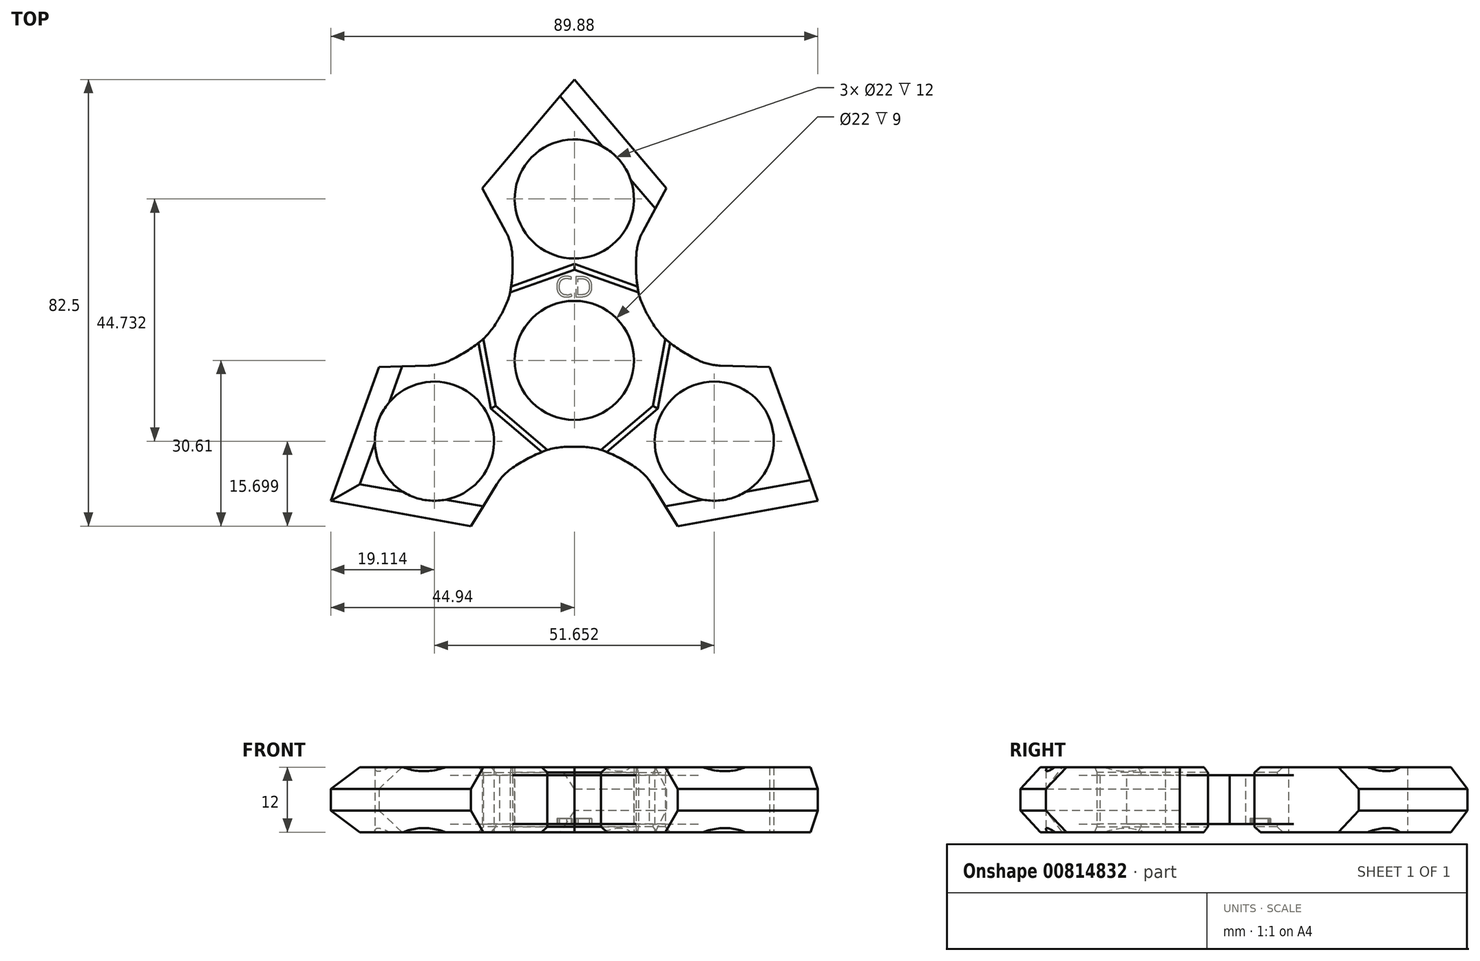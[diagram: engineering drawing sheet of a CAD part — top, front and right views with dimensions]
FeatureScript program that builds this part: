
annotation { "Feature Type Name" : "Feature", "Feature Type Description" : "" }
export const myFeature = defineFeature(function(context is Context, id is Id, definition is map)
    precondition{}
    {
        {
            var Q0;
            Q0=qCreatedBy(makeId("Top.planeOp"),FACE);
            var sketch = newSketch(context, id + "F0", { "sketchPlane" : qUnion([Q0])});
            skCircle(sketch, "E0", {"center": v(0, 0) * mm, "radius": 11 * mm});
            skCircle(sketch, "E1", {"center": v(0, 0) * mm, "radius": 15 * mm});
            skPoint(sketch, "E2.visualSharp", {"position": v(-8.6, 40.5) * mm});
            skPoint(sketch, "E3.MirrorP", {"position": v(8.6, 40.5) * mm});
            skLineSegment(sketch, "E4", {"start": v(0, 51.9) * mm, "end": v(-16.97, 31.83) * mm});
            skLineSegment(sketch, "E5", {"start": v(-16.97, 31.83) * mm, "end": v(-12.64, 23.8) * mm});
            skLineSegment(sketch, "E6.MirrorCS", {"start": v(0, 51.9) * mm, "end": v(16.97, 31.83) * mm});
            skArc(sketch, "E7", {"start": v(-13.91, 5.61) * mm, "mid": v(-11.83, 12.55) * mm, "end": v(-11.47, 19.78) * mm});
            skLineSegment(sketch, "E8.MirrorCS", {"start": v(16.97, 31.83) * mm, "end": v(12.64, 23.8) * mm});
            skArc(sketch, "E9.MirrorCS", {"start": v(13.91, 5.61) * mm, "mid": v(11.83, 12.55) * mm, "end": v(11.47, 19.78) * mm});
            skPoint(sketch, "E10.visualSharp", {"position": v(-11.73, 22.12) * mm});
            skArc(sketch, "E10.filletArc", {"start": v(-11.47, 19.78) * mm, "mid": v(-11.84, 21.85) * mm, "end": v(-12.64, 23.8) * mm});
            skPoint(sketch, "E11.visualSharp", {"position": v(11.73, 22.12) * mm});
            skArc(sketch, "E11.filletArc", {"start": v(12.64, 23.8) * mm, "mid": v(11.84, 21.85) * mm, "end": v(11.47, 19.78) * mm});
            skPoint(sketch, "E12.1.1", {"position": v(-30.77, -27.69) * mm});
            skPoint(sketch, "E12.1.2", {"position": v(-13.29, -21.22) * mm});
            skPoint(sketch, "E12.1.4", {"position": v(-25.02, -0.9) * mm});
            skLineSegment(sketch, "E12.1.5", {"start": v(-44.94, -25.95) * mm, "end": v(-36.05, -1.22) * mm});
            skLineSegment(sketch, "E12.1.6", {"start": v(-36.05, -1.22) * mm, "end": v(-26.94, -0.95) * mm});
            skLineSegment(sketch, "E12.1.7", {"start": v(-19.08, -30.6) * mm, "end": v(-14.3, -22.85) * mm});
            skLineSegment(sketch, "E12.1.9", {"start": v(-44.94, -25.95) * mm, "end": v(-19.08, -30.6) * mm});
            skPoint(sketch, "E12.1.10", {"position": v(-39.36, -12.8) * mm});
            skArc(sketch, "E12.1.12", {"start": v(-26.94, -0.95) * mm, "mid": v(-24.85, -0.67) * mm, "end": v(-22.86, 0.04) * mm});
            skArc(sketch, "E12.1.13", {"start": v(-11.4, -19.82) * mm, "mid": v(-13, -21.18) * mm, "end": v(-14.3, -22.85) * mm});
            skArc(sketch, "E12.1.14", {"start": v(2.1, -14.85) * mm, "mid": v(-4.95, -16.51) * mm, "end": v(-11.4, -19.82) * mm});
            skArc(sketch, "E12.1.15", {"start": v(-11.82, 9.24) * mm, "mid": v(-16.78, 3.97) * mm, "end": v(-22.86, 0.04) * mm});
            skPoint(sketch, "E12.2.1", {"position": v(39.36, -12.8) * mm});
            skPoint(sketch, "E12.2.2", {"position": v(25.02, -0.9) * mm});
            skPoint(sketch, "E12.2.4", {"position": v(13.29, -21.22) * mm});
            skLineSegment(sketch, "E12.2.5", {"start": v(44.94, -25.95) * mm, "end": v(19.08, -30.6) * mm});
            skLineSegment(sketch, "E12.2.6", {"start": v(19.08, -30.6) * mm, "end": v(14.3, -22.85) * mm});
            skLineSegment(sketch, "E12.2.7", {"start": v(36.05, -1.22) * mm, "end": v(26.94, -0.95) * mm});
            skLineSegment(sketch, "E12.2.9", {"start": v(44.94, -25.95) * mm, "end": v(36.05, -1.22) * mm});
            skPoint(sketch, "E12.2.10", {"position": v(30.77, -27.69) * mm});
            skArc(sketch, "E12.2.12", {"start": v(14.3, -22.85) * mm, "mid": v(13, -21.18) * mm, "end": v(11.4, -19.82) * mm});
            skArc(sketch, "E12.2.13", {"start": v(22.86, 0.04) * mm, "mid": v(24.85, -0.67) * mm, "end": v(26.94, -0.95) * mm});
            skArc(sketch, "E12.2.14", {"start": v(11.82, 9.24) * mm, "mid": v(16.78, 3.97) * mm, "end": v(22.86, 0.04) * mm});
            skArc(sketch, "E12.2.15", {"start": v(-2.1, -14.85) * mm, "mid": v(4.95, -16.51) * mm, "end": v(11.4, -19.82) * mm});
            skArc(sketch, "E13", {"start": v(0, -15.94) * mm, "mid": v(-2.5, -16.04) * mm, "end": v(-4.95, -16.51) * mm});
            skArc(sketch, "E14.MirrorCS", {"start": v(0, -15.94) * mm, "mid": v(2.5, -16.04) * mm, "end": v(4.95, -16.51) * mm});
            skArc(sketch, "E15.1.1", {"start": v(13.8, 7.97) * mm, "mid": v(12.64, 10.18) * mm, "end": v(11.83, 12.55) * mm});
            skArc(sketch, "E15.1.2", {"start": v(13.8, 7.97) * mm, "mid": v(15.14, 5.85) * mm, "end": v(16.78, 3.97) * mm});
            skArc(sketch, "E15.2.1", {"start": v(-13.8, 7.97) * mm, "mid": v(-15.14, 5.85) * mm, "end": v(-16.78, 3.97) * mm});
            skArc(sketch, "E15.2.2", {"start": v(-13.8, 7.97) * mm, "mid": v(-12.64, 10.18) * mm, "end": v(-11.83, 12.55) * mm});
            skCircle(sketch, "E16", {"center": v(0, 29.82) * mm, "radius": 11 * mm});
            skCircle(sketch, "E17.1.0", {"center": v(-25.83, -14.91) * mm, "radius": 11 * mm});
            skCircle(sketch, "E17.2.0", {"center": v(25.83, -14.91) * mm, "radius": 11 * mm});
            skSolve(sketch);
        }
        {
            var Q0;
            Q0 = qSketchRegion(id + "F0", true);
            extrude(context, id + "F1", {"entities" : qUnion([Q0]), "depth" : 9 * mm, "offsetDistance" : 25 * mm});
        }
        {
            var Q0;
            Q0=makeQuery(id+"F4rAhD535oqGD43_1.opFillet","SPLIT",FACE,{"disambiguationData":[OD(0.0)],"derivedFrom":makeQuery(id+"FJmebITgFN1S2HH_1.opChamfer","SPLIT",FACE,{"disambiguationData":[OD(3.0)],"derivedFrom":makeQuery(id+"F1.opExtrude","CAP_FACE",FACE,{"disambiguationData":[OSD([sQuery(id+"F0.wireOp",EDGE,"E1"),sQuery(id+"F0.wireOp",EDGE,"wFqUF3aU-xvko-5oIi-hobR-WI0LvXs7SEYY"),sQuery(id+"F0.wireOp",EDGE,"E4"),sQuery(id+"F0.wireOp",EDGE,"E5"),sQuery(id+"F0.wireOp",EDGE,"E6.MirrorCS"),sQuery(id+"F0.wireOp",EDGE,"E7"),sQuery(id+"F0.wireOp",EDGE,"E8.MirrorCS"),sQuery(id+"F0.wireOp",EDGE,"E9.MirrorCS"),sQuery(id+"F0.wireOp",EDGE,"E10.filletArc"),sQuery(id+"F0.wireOp",EDGE,"E11.filletArc"),sQuery(id+"F0.wireOp",EDGE,"xOrXqrbk-GGfu-HfVZ-Al4d-8NAzLdtHC7hU"),sQuery(id+"F0.wireOp",EDGE,"3626fe40-44d3-4f9b-b4e5-6d0232d855d70.MirrorCS"),sQuery(id+"F0.wireOp",EDGE,"E12.1.3"),sQuery(id+"F0.wireOp",EDGE,"E12.1.5"),sQuery(id+"F0.wireOp",EDGE,"E12.1.6"),sQuery(id+"F0.wireOp",EDGE,"E12.1.7"),sQuery(id+"F0.wireOp",EDGE,"E12.1.8"),sQuery(id+"F0.wireOp",EDGE,"E12.1.9"),sQuery(id+"F0.wireOp",EDGE,"E12.1.11"),sQuery(id+"F0.wireOp",EDGE,"E12.1.12"),sQuery(id+"F0.wireOp",EDGE,"E12.1.13"),sQuery(id+"F0.wireOp",EDGE,"E12.1.14"),sQuery(id+"F0.wireOp",EDGE,"E12.1.15"),sQuery(id+"F0.wireOp",EDGE,"E12.2.3"),sQuery(id+"F0.wireOp",EDGE,"E12.2.5"),sQuery(id+"F0.wireOp",EDGE,"E12.2.6"),sQuery(id+"F0.wireOp",EDGE,"E12.2.7"),sQuery(id+"F0.wireOp",EDGE,"E12.2.8"),sQuery(id+"F0.wireOp",EDGE,"E12.2.9"),sQuery(id+"F0.wireOp",EDGE,"E12.2.11"),sQuery(id+"F0.wireOp",EDGE,"E12.2.12"),sQuery(id+"F0.wireOp",EDGE,"E12.2.13"),sQuery(id+"F0.wireOp",EDGE,"E12.2.14"),sQuery(id+"F0.wireOp",EDGE,"E12.2.15"),sQuery(id+"F0.wireOp",EDGE,"E13"),sQuery(id+"F0.wireOp",EDGE,"E14.MirrorCS"),sQuery(id+"F0.wireOp",EDGE,"E15.1.1"),sQuery(id+"F0.wireOp",EDGE,"E15.1.2"),sQuery(id+"F0.wireOp",EDGE,"E15.2.1"),sQuery(id+"F0.wireOp",EDGE,"E15.2.2")])],"isStart":false})})});
            var sketch = newSketch(context, id + "F2", { "sketchPlane" : qUnion([Q0])});
            skCircle(sketch, "E18", {"center": v(0, 0) * mm, "radius": 11 * mm});
            skCircle(sketch, "E19", {"center": v(0, 0) * mm, "radius": 15.25 * mm});
            skSolve(sketch);
        }
        {
            var Q0;
            Q0 = qSketchRegion(id + "F2", true);
            extrude(context, id + "F3", {"entities" : qUnion([Q0]), "operationType" : NewBodyOperationType.ADD, "oppositeDirection" : true, "depth" : 9 * mm, "offsetDistance" : 25 * mm});
        }
        {
            var Q0;
            Q0=makeQuery(id+"F3.boolean.opBoolean","MERGE",FACE,{"derivedFrom":[makeQuery(id+"F1.opExtrude","CAP_FACE",FACE,{"disambiguationData":[OSD([sQuery(id+"F0.wireOp",EDGE,"E1"),sQuery(id+"F0.wireOp",EDGE,"E4"),sQuery(id+"F0.wireOp",EDGE,"E5"),sQuery(id+"F0.wireOp",EDGE,"E6.MirrorCS"),sQuery(id+"F0.wireOp",EDGE,"E7"),sQuery(id+"F0.wireOp",EDGE,"E8.MirrorCS"),sQuery(id+"F0.wireOp",EDGE,"E9.MirrorCS"),sQuery(id+"F0.wireOp",EDGE,"E10.filletArc"),sQuery(id+"F0.wireOp",EDGE,"E11.filletArc"),sQuery(id+"F0.wireOp",EDGE,"E12.1.5"),sQuery(id+"F0.wireOp",EDGE,"E12.1.6"),sQuery(id+"F0.wireOp",EDGE,"E12.1.7"),sQuery(id+"F0.wireOp",EDGE,"E12.1.9"),sQuery(id+"F0.wireOp",EDGE,"E12.1.12"),sQuery(id+"F0.wireOp",EDGE,"E12.1.13"),sQuery(id+"F0.wireOp",EDGE,"E12.1.14"),sQuery(id+"F0.wireOp",EDGE,"E12.1.15"),sQuery(id+"F0.wireOp",EDGE,"E12.2.5"),sQuery(id+"F0.wireOp",EDGE,"E12.2.6"),sQuery(id+"F0.wireOp",EDGE,"E12.2.7"),sQuery(id+"F0.wireOp",EDGE,"E12.2.9"),sQuery(id+"F0.wireOp",EDGE,"E12.2.12"),sQuery(id+"F0.wireOp",EDGE,"E12.2.13"),sQuery(id+"F0.wireOp",EDGE,"E12.2.14"),sQuery(id+"F0.wireOp",EDGE,"E12.2.15"),sQuery(id+"F0.wireOp",EDGE,"E13"),sQuery(id+"F0.wireOp",EDGE,"E14.MirrorCS"),sQuery(id+"F0.wireOp",EDGE,"E15.1.1"),sQuery(id+"F0.wireOp",EDGE,"E15.1.2"),sQuery(id+"F0.wireOp",EDGE,"E15.2.1"),sQuery(id+"F0.wireOp",EDGE,"E15.2.2"),sQuery(id+"F0.wireOp",EDGE,"E16"),sQuery(id+"F0.wireOp",EDGE,"E17.1.0"),sQuery(id+"F0.wireOp",EDGE,"E17.2.0")])],"isStart":false}),makeQuery(id+"F3.opExtrude","CAP_FACE",FACE,{"disambiguationData":[OSD([sQuery(id+"F2.wireOp",EDGE,"E18"),sQuery(id+"F2.wireOp",EDGE,"E19")])],"isStart":true})]});
            var sketch = newSketch(context, id + "F4", { "sketchPlane" : qUnion([Q0])});
            skLineSegment(sketch, "E20", {"start": v(-36.05, -1.22) * mm, "end": v(-44.94, -25.95) * mm});
            skLineSegment(sketch, "E21", {"start": v(-26.94, -0.95) * mm, "end": v(-36.05, -1.22) * mm});
            skArc(sketch, "E22", {"start": v(-26.94, -0.95) * mm, "mid": v(-24.85, -0.67) * mm, "end": v(-22.86, 0.04) * mm});
            skArc(sketch, "E23", {"start": v(-22.86, 0.04) * mm, "mid": v(-19.7, 1.8) * mm, "end": v(-16.78, 3.97) * mm});
            skArc(sketch, "E24.MirrorCS", {"start": v(-11.4, -19.82) * mm, "mid": v(-8.28, -17.96) * mm, "end": v(-4.95, -16.51) * mm});
            skArc(sketch, "E25.MirrorCS", {"start": v(-14.3, -22.85) * mm, "mid": v(-13, -21.18) * mm, "end": v(-11.4, -19.82) * mm});
            skLineSegment(sketch, "E26.MirrorCS", {"start": v(-14.3, -22.85) * mm, "end": v(-19.08, -30.6) * mm});
            skLineSegment(sketch, "E27.MirrorCS", {"start": v(-19.08, -30.6) * mm, "end": v(-44.94, -25.95) * mm});
            skLineSegment(sketch, "E28", {"start": v(-16.78, 3.97) * mm, "end": v(-14.5, -8.37) * mm});
            skLineSegment(sketch, "E29", {"start": v(-14.5, -8.37) * mm, "end": v(-4.95, -16.51) * mm});
            skCircle(sketch, "E30", {"center": v(-25.83, -14.91) * mm, "radius": 11 * mm});
            skLineSegment(sketch, "E31.1.0", {"start": v(19.08, -30.6) * mm, "end": v(44.94, -25.95) * mm});
            skLineSegment(sketch, "E31.1.1", {"start": v(26.94, -0.95) * mm, "end": v(36.05, -1.22) * mm});
            skLineSegment(sketch, "E31.1.2", {"start": v(14.5, -8.37) * mm, "end": v(16.78, 3.97) * mm});
            skCircle(sketch, "E31.1.3", {"center": v(25.83, -14.91) * mm, "radius": 11 * mm});
            skArc(sketch, "E31.1.4", {"start": v(14.3, -22.85) * mm, "mid": v(13, -21.18) * mm, "end": v(11.4, -19.82) * mm});
            skLineSegment(sketch, "E31.1.5", {"start": v(36.05, -1.22) * mm, "end": v(44.94, -25.95) * mm});
            skLineSegment(sketch, "E31.1.6", {"start": v(4.95, -16.51) * mm, "end": v(14.5, -8.37) * mm});
            skArc(sketch, "E31.1.7", {"start": v(11.4, -19.82) * mm, "mid": v(8.28, -17.96) * mm, "end": v(4.95, -16.51) * mm});
            skLineSegment(sketch, "E31.1.8", {"start": v(14.3, -22.85) * mm, "end": v(19.08, -30.6) * mm});
            skArc(sketch, "E31.1.9", {"start": v(26.94, -0.95) * mm, "mid": v(24.85, -0.67) * mm, "end": v(22.86, 0.04) * mm});
            skArc(sketch, "E31.1.10", {"start": v(22.86, 0.04) * mm, "mid": v(19.7, 1.8) * mm, "end": v(16.78, 3.97) * mm});
            skLineSegment(sketch, "E31.1.11", {"start": v(36.05, -1.22) * mm, "end": v(44.94, -25.95) * mm});
            skLineSegment(sketch, "E31.1.12", {"start": v(36.05, -1.22) * mm, "end": v(44.94, -25.95) * mm});
            skLineSegment(sketch, "E31.2.0", {"start": v(16.97, 31.83) * mm, "end": v(0, 51.9) * mm});
            skLineSegment(sketch, "E31.2.1", {"start": v(-12.64, 23.8) * mm, "end": v(-16.97, 31.83) * mm});
            skLineSegment(sketch, "E31.2.2", {"start": v(0, 16.75) * mm, "end": v(-11.83, 12.55) * mm});
            skCircle(sketch, "E31.2.3", {"center": v(0, 29.82) * mm, "radius": 11 * mm});
            skArc(sketch, "E31.2.4", {"start": v(12.64, 23.8) * mm, "mid": v(11.84, 21.85) * mm, "end": v(11.47, 19.78) * mm});
            skLineSegment(sketch, "E31.2.5", {"start": v(-16.97, 31.83) * mm, "end": v(0, 51.9) * mm});
            skLineSegment(sketch, "E31.2.6", {"start": v(11.83, 12.55) * mm, "end": v(0, 16.75) * mm});
            skArc(sketch, "E31.2.7", {"start": v(11.47, 19.78) * mm, "mid": v(11.41, 16.15) * mm, "end": v(11.83, 12.55) * mm});
            skLineSegment(sketch, "E31.2.8", {"start": v(12.64, 23.8) * mm, "end": v(16.97, 31.83) * mm});
            skArc(sketch, "E31.2.9", {"start": v(-12.64, 23.8) * mm, "mid": v(-11.84, 21.85) * mm, "end": v(-11.47, 19.78) * mm});
            skArc(sketch, "E31.2.10", {"start": v(-11.47, 19.78) * mm, "mid": v(-11.41, 16.15) * mm, "end": v(-11.83, 12.55) * mm});
            skLineSegment(sketch, "E31.2.11", {"start": v(-16.97, 31.83) * mm, "end": v(0, 51.9) * mm});
            skLineSegment(sketch, "E31.2.12", {"start": v(-16.97, 31.83) * mm, "end": v(0, 51.9) * mm});
            skPoint(sketch, "E31.center", {"position": v(0, 0) * mm});
            skSolve(sketch);
        }
        {
            var Q0;
            Q0 = qSketchRegion(id + "F4", true);
            extrude(context, id + "F5", {"entities" : qUnion([Q0]), "operationType" : NewBodyOperationType.ADD, "depth" : 1.5 * mm, "offsetDistance" : 25 * mm, "hasSecondDirection" : true, "secondDirectionOppositeDirection" : true, "secondDirectionDepth" : 10.5 * mm});
        }
        {
            var Q0;
            Q0=makeQuery(id+"F5.opExtrude","CAP_EDGE",EDGE,{"disambiguationData":[OSD([sQuery(id+"F4.wireOp",EDGE,"E28")])],"isStart":false});
            var Q1;
            Q1=makeQuery(id+"F5.opExtrude","CAP_EDGE",EDGE,{"disambiguationData":[OSD([sQuery(id+"F4.wireOp",EDGE,"E29")])],"isStart":false});
            var Q2;
            Q2=makeQuery(id+"F5.opExtrude","CAP_EDGE",EDGE,{"disambiguationData":[OSD([sQuery(id+"F4.wireOp",EDGE,"E29")])],"isStart":true});
            var Q3;
            Q3=makeQuery(id+"F5.opExtrude","CAP_EDGE",EDGE,{"disambiguationData":[OSD([sQuery(id+"F4.wireOp",EDGE,"E28")])],"isStart":true});
            var Q4;
            Q4=makeQuery(id+"F5.opExtrude","CAP_EDGE",EDGE,{"disambiguationData":[OSD([sQuery(id+"F4.wireOp",EDGE,"E31.1.6")])],"isStart":true});
            var Q5;
            Q5=makeQuery(id+"F5.opExtrude","CAP_EDGE",EDGE,{"disambiguationData":[OSD([sQuery(id+"F4.wireOp",EDGE,"E31.1.2")])],"isStart":true});
            var Q6;
            Q6=makeQuery(id+"F5.opExtrude","CAP_EDGE",EDGE,{"disambiguationData":[OSD([sQuery(id+"F4.wireOp",EDGE,"E31.2.6")])],"isStart":true});
            var Q7;
            Q7=makeQuery(id+"F5.opExtrude","CAP_EDGE",EDGE,{"disambiguationData":[OSD([sQuery(id+"F4.wireOp",EDGE,"E31.2.2")])],"isStart":true});
            var Q8;
            Q8=makeQuery(id+"F5.opExtrude","CAP_EDGE",EDGE,{"disambiguationData":[OSD([sQuery(id+"F4.wireOp",EDGE,"E31.1.2")])],"isStart":false});
            var Q9;
            Q9=makeQuery(id+"F5.opExtrude","CAP_EDGE",EDGE,{"disambiguationData":[OSD([sQuery(id+"F4.wireOp",EDGE,"E31.1.6")])],"isStart":false});
            var Q10;
            Q10=makeQuery(id+"F5.opExtrude","CAP_EDGE",EDGE,{"disambiguationData":[OSD([sQuery(id+"F4.wireOp",EDGE,"E31.2.6")])],"isStart":false});
            var Q11;
            Q11=makeQuery(id+"F5.opExtrude","CAP_EDGE",EDGE,{"disambiguationData":[OSD([sQuery(id+"F4.wireOp",EDGE,"E31.2.2")])],"isStart":false});
            chamfer(context, id + "F6", {"entities" : qUnion([Q0, Q1, Q2, Q3, Q4, Q5, Q6, Q7, Q8, Q9, Q10, Q11]), "width" : 1 * mm, "tangentPropagation" : true});
        }
        {
            var Q0;
            Q0=makeQuery(id+"F5.opExtrude","CAP_EDGE",EDGE,{"disambiguationData":[OSD([sQuery(id+"F4.wireOp",EDGE,"E27.MirrorCS")])],"isStart":false});
            var Q1;
            Q1=makeQuery(id+"F5.opExtrude","CAP_EDGE",EDGE,{"disambiguationData":[OSD([sQuery(id+"F4.wireOp",EDGE,"E20")])],"isStart":false});
            var Q2;
            Q2=makeQuery(id+"F5.opExtrude","CAP_EDGE",EDGE,{"disambiguationData":[OSD([sQuery(id+"F4.wireOp",EDGE,"E27.MirrorCS")])],"isStart":true});
            var Q3;
            Q3=makeQuery(id+"F5.opExtrude","CAP_EDGE",EDGE,{"disambiguationData":[OSD([sQuery(id+"F4.wireOp",EDGE,"E20")])],"isStart":true});
            var Q4;
            Q4=makeQuery(id+"F5.opExtrude","CAP_EDGE",EDGE,{"disambiguationData":[OSD([sQuery(id+"F4.wireOp",EDGE,"E31.1.0")])],"isStart":false});
            var Q5;
            Q5=makeQuery(id+"F5.opExtrude","CAP_EDGE",EDGE,{"disambiguationData":[OSD([sQuery(id+"F4.wireOp",EDGE,"E31.1.0")])],"isStart":true});
            var Q6;
            Q6=makeQuery(id+"F5.opExtrude","CAP_EDGE",EDGE,{"disambiguationData":[OSD([sQuery(id+"F4.wireOp",EDGE,"E31.1.12")])],"isStart":false});
            var Q7;
            Q7=makeQuery(id+"F5.opExtrude","CAP_EDGE",EDGE,{"disambiguationData":[OSD([sQuery(id+"F4.wireOp",EDGE,"E31.1.12")])],"isStart":true});
            var Q8;
            Q8=makeQuery(id+"F5.opExtrude","CAP_EDGE",EDGE,{"disambiguationData":[OSD([sQuery(id+"F4.wireOp",EDGE,"E31.2.0")])],"isStart":false});
            var Q9;
            Q9=makeQuery(id+"F5.opExtrude","CAP_EDGE",EDGE,{"disambiguationData":[OSD([sQuery(id+"F4.wireOp",EDGE,"E31.2.0")])],"isStart":true});
            var Q10;
            Q10=makeQuery(id+"F5.opExtrude","CAP_EDGE",EDGE,{"disambiguationData":[OSD([sQuery(id+"F4.wireOp",EDGE,"E31.2.12")])],"isStart":true});
            var Q11;
            Q11=makeQuery(id+"F5.opExtrude","CAP_EDGE",EDGE,{"disambiguationData":[OSD([sQuery(id+"F4.wireOp",EDGE,"E31.2.12")])],"isStart":false});
            chamfer(context, id + "F7", {"entities" : qUnion([Q0, Q1, Q2, Q3, Q4, Q5, Q6, Q7, Q8, Q9, Q10, Q11]), "width" : 4 * mm, "tangentPropagation" : true});
        }
        {
            var Q0;
            {var subQ0=sQuery(id+"F2.wireOp",EDGE,"E18");var subQ1=makeQuery(id+"F3.opExtrude","CAP_FACE",FACE,{"disambiguationData":[OSD([subQ0,sQuery(id+"F2.wireOp",EDGE,"E19")])],"isStart":false});var subQ2=sQuery(id+"F0.wireOp",EDGE,"E15.2.2");var subQ3=sQuery(id+"F0.wireOp",EDGE,"E15.2.1");var subQ4=sQuery(id+"F0.wireOp",EDGE,"E15.1.2");var subQ5=sQuery(id+"F0.wireOp",EDGE,"E12.1.14");var subQ6=sQuery(id+"F0.wireOp",EDGE,"E12.1.13");var subQ7=sQuery(id+"F0.wireOp",EDGE,"E13");var subQ8=sQuery(id+"F0.wireOp",EDGE,"E15.1.1");var subQ9=sQuery(id+"F0.wireOp",EDGE,"E14.MirrorCS");var subQ10=sQuery(id+"F0.wireOp",EDGE,"E12.2.15");var subQ11=sQuery(id+"F0.wireOp",EDGE,"E12.2.14");var subQ12=sQuery(id+"F0.wireOp",EDGE,"E12.2.13");var subQ13=sQuery(id+"F0.wireOp",EDGE,"E12.2.12");var subQ14=sQuery(id+"F0.wireOp",EDGE,"E12.1.15");var subQ15=sQuery(id+"F0.wireOp",EDGE,"E12.1.12");var subQ16=sQuery(id+"F0.wireOp",EDGE,"E11.filletArc");var subQ17=sQuery(id+"F0.wireOp",EDGE,"E10.filletArc");var subQ18=sQuery(id+"F0.wireOp",EDGE,"E9.MirrorCS");var subQ19=sQuery(id+"F0.wireOp",EDGE,"E7");var subQ20=makeQuery(id+"F1.opExtrude","CAP_FACE",FACE,{"disambiguationData":[OSD([sQuery(id+"F0.wireOp",EDGE,"E1"),sQuery(id+"F0.wireOp",EDGE,"E4"),sQuery(id+"F0.wireOp",EDGE,"E5"),sQuery(id+"F0.wireOp",EDGE,"E6.MirrorCS"),subQ19,sQuery(id+"F0.wireOp",EDGE,"E8.MirrorCS"),subQ18,subQ17,subQ16,sQuery(id+"F0.wireOp",EDGE,"E12.1.5"),sQuery(id+"F0.wireOp",EDGE,"E12.1.6"),sQuery(id+"F0.wireOp",EDGE,"E12.1.7"),sQuery(id+"F0.wireOp",EDGE,"E12.1.9"),subQ15,subQ6,subQ5,subQ14,sQuery(id+"F0.wireOp",EDGE,"E12.2.5"),sQuery(id+"F0.wireOp",EDGE,"E12.2.6"),sQuery(id+"F0.wireOp",EDGE,"E12.2.7"),sQuery(id+"F0.wireOp",EDGE,"E12.2.9"),subQ13,subQ12,subQ11,subQ10,subQ7,subQ9,subQ8,subQ4,subQ3,subQ2,sQuery(id+"F0.wireOp",EDGE,"E16"),sQuery(id+"F0.wireOp",EDGE,"E17.1.0"),sQuery(id+"F0.wireOp",EDGE,"E17.2.0")])],"isStart":true});Q0=makeQuery(id+"F5.boolean.opBoolean","SPLIT",FACE,{"disambiguationData":[TD([makeQuery(id+"F3.opExtrude","SWEPT_FACE",FACE,{"disambiguationData":[OSD([subQ0])]})])],"derivedFrom":makeQuery(id+"F3.boolean.opBoolean","MERGE",FACE,{"derivedFrom":[subQ20,subQ1]})});}
            var sketch = newSketch(context, id + "F8", { "sketchPlane" : qUnion([Q0])});
            skText(sketch, "E32", { "text": "CD", "fontName": "OpenSans-Regular.ttf"});
            const initialGuessF8  = {"E32": [-0.00355, -0.01549, 1, 0, 0.00376]};
            skSetInitialGuess(sketch, initialGuessF8);
            skSolve(sketch);
        }
        {
            var Q0;
            Q0 = qSketchRegion(id + "F8", true);
            extrude(context, id + "F9", {"entities" : qUnion([Q0]), "operationType" : NewBodyOperationType.REMOVE, "oppositeDirection" : true, "depth" : 1 * mm, "offsetDistance" : 25 * mm});
        }
    });
